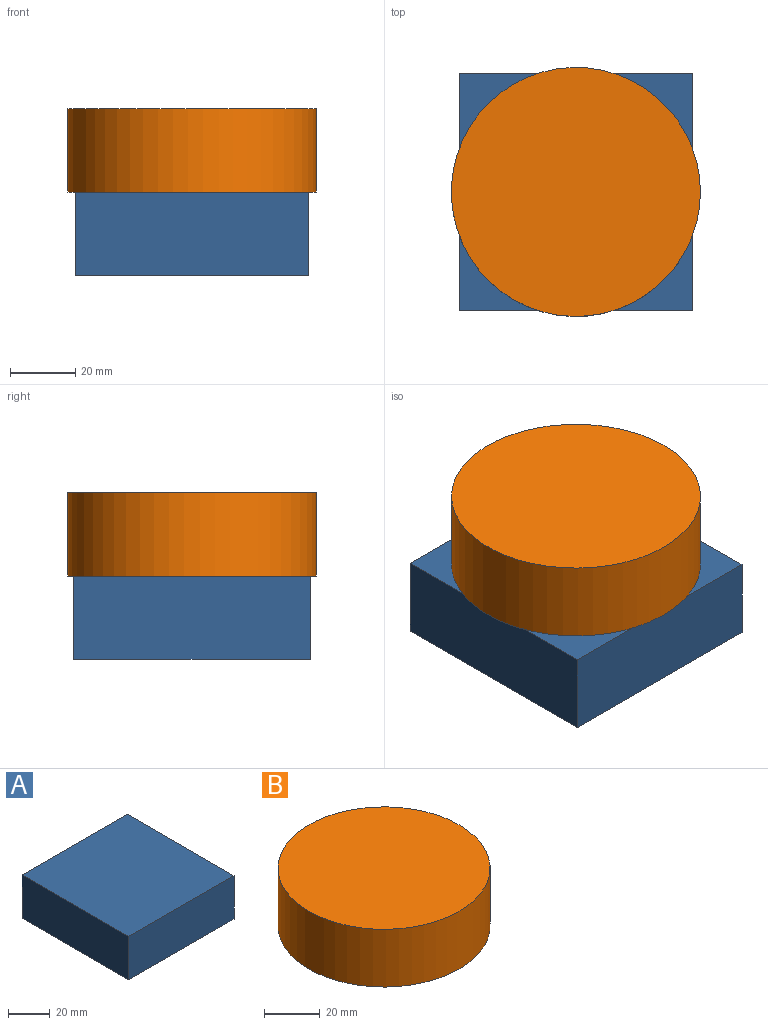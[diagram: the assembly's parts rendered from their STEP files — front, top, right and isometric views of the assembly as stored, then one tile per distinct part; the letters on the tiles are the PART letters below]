
ASSEMBLY  parts=2 mates=1
PART A: 6 faces, bbox 71.3x72.4x25.4 mm
  f0: plane 71.33x25.4mm, normal (0,1,0), area 1811.8mm2, adj f1,f3,f4,f5
  f1: plane 72.35x25.4mm, normal (-1,0,0), area 1837.7mm2, adj f0,f2,f4,f5
  f2: plane 71.33x25.4mm, normal (0,-1,0), area 1811.8mm2, adj f1,f3,f4,f5
  f3: plane 72.35x25.4mm, normal (1,0,0), area 1837.7mm2, adj f0,f2,f4,f5
  f4: plane 72.35x71.33mm, normal (0,0,1), area 5160.8mm2, adj f0,f1,f2,f3
  f5: plane 72.35x71.33mm, normal (0,0,-1), area 5160.8mm2, adj f0,f1,f2,f3
PART B: 3 faces, bbox 76.2x76.2x25.4 mm
  f0: cylinder r=38.1mm len=76.2mm, axis (0,0,-1), area 6080.5mm2, adj f1,f2
  f1: plane 76.2x76.2mm, normal (0,0,1), area 4560.4mm2, adj f0
  f2: plane 76.2x76.2mm, normal (0,0,-1), area 4560.4mm2, adj f0
PLACE A at identity
PLACE B rot(axis=(1,0,0),180deg) t=(0,0,50.8)mm
MATE fastened B.f0 <-> A.f4  axis (0,0,-1) through (0,0,25.4)mm
